# Revit family: Rohrschelle Trabant Inox, M 8-M10, ohne Dämmung, V4A
name_source: partatom
category: HLS-Bauteile
revit_build: Autodesk Revit 2017 (Build: 20190507_1515(x64)
units: mm (PartAtom-declared; Revit-internal decimal feet)

## family parameters
Arbeitsebenenbasiert = Ja
Beim Laden mit Abzugskörper schneiden = Nein
Bemaßung runder Anschluss = Durchmesser verwenden
Gemeinsam genutzt = Ja
Immer vertikal = Nein
Raumberechnungspunkt = Nein
Teiletyp = Normal

## types (11) — shared parameters
Anschluss = M8/M10
Bauart = zweiteilig
DF2 = 16 mm  [stored 0.0524934 ft]
DVS = 5 mm  [stored 0.0164042 ft]
Fabrikat = MEFA
Firma = MEFA Befestigungs- und Montagesysteme GmbH
H1 = 2 mm  [stored 0.00656168 ft]
HGA = 17 mm
Material = Edelstahl
Mengeneinheit = St
Verschluss = Rastverschluss
Verschluss-Schraube = M6
Vorgabe-Ansicht = 1219 mm
max. zul. Last horizontal = 0.00 kN
max. zul. Last vertikal = 0.00 kN
zero-valued in all types: DS, Nennweite DN Rohr, Rohraußendurchmesser

## per-type parameters (varying)
- Trabant Inox, M8/M10, Ø 21- 24, o.Gummi, V4A: A=18 mm  [stored 0.0590551 ft]; AB=3 mm  [stored 0.00984252 ft]; Achsabstand=42,0 mm; Anschlußhöhe=17,5 mm; Artikelnummer=051005024; B=59 mm; Breite Material=20 mm; D=24 mm  [stored 0.0787402 ft]; D0=24 mm  [stored 0.0787402 ft]; DF1=17 mm; Dmax=24 mm  [stored 0.0787402 ft]; Dmin=21 mm  [stored 0.0688976 ft]; EAN=4250928454003; Gewicht=0.05 kg; Gewicht pro Bauteil=0.05 kg; H=43 mm  [stored 0.141076 ft]; H2=4 mm  [stored 0.0131234 ft]; Kurztext1=Rohrschelle Trabant Inox 20x1,0; Kurztext2=21 - 24 mm M8/M10; MB=20 mm  [stored 0.0656168 ft]; MD=1 mm  [stored 0.00328084 ft]; Materialmaße=20x1,0 mm; R=12 mm  [stored 0.0393701 ft]; RM=15 mm  [stored 0.0492126 ft]; Rohraußendurchmesser Zoll=1/2 Zoll; S=42 mm  [stored 0.137795 ft]; Stärke Material=1 mm  [stored 0.00328084 ft]; max. Rohraußendurchmesser=24 mm  [stored 0.0787402 ft]; min. Rohraußendurchmesser=21 mm  [stored 0.0688976 ft]; vpe=100 St
- Trabant Inox, M8/M10, Ø 25- 29, o.Gummi, V4A: A=18 mm  [stored 0.0590551 ft]; AB=4 mm  [stored 0.0131234 ft]; Achsabstand=46,5 mm; Anschlußhöhe=17,5 mm; Artikelnummer=051005029; B=64 mm; Breite Material=20 mm; D=29 mm  [stored 0.0951444 ft]; D0=29 mm  [stored 0.0951444 ft]; DF1=17 mm; Dmax=29 mm  [stored 0.0951444 ft]; Dmin=25 mm  [stored 0.082021 ft]; EAN=4250928454010; Gewicht=0.05 kg; Gewicht pro Bauteil=0.05 kg; H=48 mm  [stored 0.15748 ft]; H2=5 mm  [stored 0.0164042 ft]; Kurztext1=Rohrschelle Trabant Inox 20x1,0; Kurztext2=25 - 29 mm M8/M10; MB=20 mm  [stored 0.0656168 ft]; MD=1 mm  [stored 0.00328084 ft]; Materialmaße=20x1,0 mm; R=15 mm  [stored 0.0492126 ft]; RM=18 mm  [stored 0.0590551 ft]; Rohraußendurchmesser Zoll=3/4 Zoll; S=47 mm  [stored 0.154199 ft]; Stärke Material=1 mm  [stored 0.00328084 ft]; max. Rohraußendurchmesser=29 mm  [stored 0.0951444 ft]; min. Rohraußendurchmesser=25 mm  [stored 0.082021 ft]; vpe=100 St
- Trabant Inox, M8/M10, Ø 30- 34, o.Gummi, V4A: A=18 mm  [stored 0.0590551 ft]; AB=4 mm  [stored 0.0131234 ft]; Achsabstand=51,5 mm; Anschlußhöhe=17,5 mm; Artikelnummer=051005034; B=69 mm; Breite Material=20 mm; D=34 mm  [stored 0.111549 ft]; D0=34 mm  [stored 0.111549 ft]; DF1=17 mm; Dmax=34 mm  [stored 0.111549 ft]; Dmin=30 mm  [stored 0.0984252 ft]; EAN=4250928454027; Gewicht=0.05 kg; Gewicht pro Bauteil=0.05 kg; H=53 mm; H2=5 mm  [stored 0.0164042 ft]; Kurztext1=Rohrschelle Trabant Inox 20x1,0; Kurztext2=30 - 34 mm M8/M10; MB=20 mm  [stored 0.0656168 ft]; MD=1 mm  [stored 0.00328084 ft]; Materialmaße=20x1,0 mm; R=17 mm; RM=20 mm  [stored 0.0656168 ft]; Rohraußendurchmesser Zoll=1 Zoll; S=52 mm; Stärke Material=1 mm  [stored 0.00328084 ft]; max. Rohraußendurchmesser=34 mm  [stored 0.111549 ft]; min. Rohraußendurchmesser=30 mm  [stored 0.0984252 ft]; vpe=100 St
- Trabant Inox, M8/M10, Ø 35- 39, o.Gummi, V4A: A=18 mm  [stored 0.0590551 ft]; AB=4 mm  [stored 0.0131234 ft]; Achsabstand=57,0 mm; Anschlußhöhe=17,5 mm; Artikelnummer=051005039; B=74 mm; Breite Material=20 mm; D=39 mm  [stored 0.127953 ft]; D0=39 mm  [stored 0.127953 ft]; DF1=17 mm; Dmax=39 mm  [stored 0.127953 ft]; Dmin=35 mm  [stored 0.114829 ft]; EAN=4250928454034; Gewicht=0.05 kg; Gewicht pro Bauteil=0.05 kg; H=58 mm; H2=5 mm  [stored 0.0164042 ft]; Kurztext1=Rohrschelle Trabant Inox 20x1,0; Kurztext2=35 - 39 mm M8/M10; MB=20 mm  [stored 0.0656168 ft]; MD=1 mm  [stored 0.00328084 ft]; Materialmaße=20x1,0 mm; R=20 mm  [stored 0.0656168 ft]; RM=23 mm; S=57 mm; Stärke Material=1 mm  [stored 0.00328084 ft]; max. Rohraußendurchmesser=39 mm  [stored 0.127953 ft]; min. Rohraußendurchmesser=35 mm  [stored 0.114829 ft]; vpe=100 St
- Trabant Inox, M8/M10, Ø 41- 48, o.Gummi, V4A: A=18 mm  [stored 0.0590551 ft]; AB=7 mm  [stored 0.0229659 ft]; Achsabstand=65,0 mm; Anschlußhöhe=17,5 mm; Artikelnummer=051005048; B=83 mm; Breite Material=20 mm; D=48 mm  [stored 0.15748 ft]; D0=48 mm  [stored 0.15748 ft]; DF1=17 mm; Dmax=48 mm  [stored 0.15748 ft]; Dmin=41 mm  [stored 0.134514 ft]; EAN=4250928454041; Gewicht=0.06 kg; Gewicht pro Bauteil=0.06 kg; H=67 mm; H2=6 mm  [stored 0.019685 ft]; Kurztext1=Rohrschelle Trabant Inox 20x1,0; Kurztext2=41 - 48 mm M8/M10; MB=20 mm  [stored 0.0656168 ft]; MD=1 mm  [stored 0.00328084 ft]; Materialmaße=20x1,0 mm; R=24 mm  [stored 0.0787402 ft]; RM=29 mm  [stored 0.0951444 ft]; Rohraußendurchmesser Zoll=1 1/4 Zoll; S=66 mm; Stärke Material=1 mm  [stored 0.00328084 ft]; max. Rohraußendurchmesser=48 mm  [stored 0.15748 ft]; min. Rohraußendurchmesser=41 mm  [stored 0.134514 ft]; vpe=100 St
- Trabant Inox, M8/M10, Ø 51- 55, o.Gummi, V4A: A=19 mm; AB=4 mm  [stored 0.0131234 ft]; Achsabstand=74,0 mm; Anschlußhöhe=18 mm; Artikelnummer=051005055; B=92 mm; Breite Material=20 mm; D=55 mm; D0=55 mm; DF1=18 mm  [stored 0.0590551 ft]; Dmax=55 mm; Dmin=51 mm  [stored 0.167323 ft]; EAN=4250928454058; Gewicht=0.08 kg; Gewicht pro Bauteil=0.08 kg; H=75 mm; H2=5 mm  [stored 0.0164042 ft]; Kurztext1=Rohrschelle Trabant Inox 20x1,5; Kurztext2=51 - 55 mm M8/M10; MB=20 mm  [stored 0.0656168 ft]; MD=2 mm  [stored 0.00656168 ft]; Materialmaße=20x1,5 mm; R=28 mm; RM=31 mm  [stored 0.101706 ft]; Rohraußendurchmesser Zoll=1 1/2 Zoll; S=74 mm; Stärke Material=2 mm  [stored 0.00656168 ft]; max. Rohraußendurchmesser=55 mm; min. Rohraußendurchmesser=51 mm  [stored 0.167323 ft]; vpe=50 St
- Trabant Inox, M8/M10, Ø 57- 61, o.Gummi, V4A: A=19 mm; AB=4 mm  [stored 0.0131234 ft]; Achsabstand=80,5 mm; Anschlußhöhe=18 mm; Artikelnummer=051005061; B=98 mm; Breite Material=20 mm; D=61 mm; D0=61 mm; DF1=18 mm  [stored 0.0590551 ft]; Dmax=61 mm; Dmin=57 mm; EAN=4250928454065; Gewicht=0.09 kg; Gewicht pro Bauteil=0.09 kg; H=81 mm; H2=5 mm  [stored 0.0164042 ft]; Kurztext1=Rohrschelle Trabant Inox 20x1,5; Kurztext2=57 - 61 mm M8/M10; MB=20 mm  [stored 0.0656168 ft]; MD=2 mm  [stored 0.00656168 ft]; Materialmaße=20x1,5 mm; R=31 mm  [stored 0.101706 ft]; RM=34 mm  [stored 0.111549 ft]; Rohraußendurchmesser Zoll=2 Zoll; S=80 mm; Stärke Material=2 mm  [stored 0.00656168 ft]; max. Rohraußendurchmesser=61 mm; min. Rohraußendurchmesser=57 mm; vpe=50 St
- Trabant Inox, M8/M10, Ø 63- 67, o.Gummi, V4A: A=19 mm; AB=4 mm  [stored 0.0131234 ft]; Achsabstand=86,5 mm; Anschlußhöhe=18 mm; Artikelnummer=051005067; B=104 mm; Breite Material=20 mm; D=67 mm; D0=67 mm; DF1=18 mm  [stored 0.0590551 ft]; Dmax=67 mm; Dmin=63 mm; EAN=4250928454072; Gewicht=0.09 kg; Gewicht pro Bauteil=0.09 kg; H=87 mm; H2=5 mm  [stored 0.0164042 ft]; Kurztext1=Rohrschelle Trabant Inox 20x1,5; Kurztext2=63 - 67 mm M8/M10; MB=20 mm  [stored 0.0656168 ft]; MD=2 mm  [stored 0.00656168 ft]; Materialmaße=20x1,5 mm; R=34 mm  [stored 0.111549 ft]; RM=37 mm  [stored 0.121391 ft]; S=86 mm; Stärke Material=2 mm  [stored 0.00656168 ft]; max. Rohraußendurchmesser=67 mm; min. Rohraußendurchmesser=63 mm; vpe=50 St
- Trabant Inox, M8/M10, Ø 69- 74, o.Gummi, V4A: A=19 mm; AB=5 mm  [stored 0.0164042 ft]; Achsabstand=93,5 mm; Anschlußhöhe=18 mm; Artikelnummer=051005074; B=111 mm; Breite Material=20 mm; D=74 mm; D0=74 mm; DF1=18 mm  [stored 0.0590551 ft]; Dmax=74 mm; Dmin=69 mm; EAN=4250928454089; Gewicht=0.10 kg; Gewicht pro Bauteil=0.10 kg; H=94 mm; H2=6 mm  [stored 0.019685 ft]; Kurztext1=Rohrschelle Trabant Inox 20x1,5; Kurztext2=69 - 74 mm M8/M10; MB=20 mm  [stored 0.0656168 ft]; MD=2 mm  [stored 0.00656168 ft]; Materialmaße=20x1,5 mm; R=37 mm  [stored 0.121391 ft]; RM=41 mm  [stored 0.134514 ft]; S=93 mm; Stärke Material=2 mm  [stored 0.00656168 ft]; max. Rohraußendurchmesser=74 mm; min. Rohraußendurchmesser=69 mm; vpe=50 St
- Trabant Inox, M8/M10, Ø 76- 85, o.Gummi, V4A: A=19 mm; AB=9 mm  [stored 0.0295276 ft]; Achsabstand=104,0 mm; Anschlußhöhe=18 mm; Artikelnummer=051005085; B=121 mm; Breite Material=25 mm; D=85 mm; D0=85 mm; DF1=17 mm; Dmax=85 mm; Dmin=76 mm; EAN=4250928454096; Gewicht=0.12 kg; Gewicht pro Bauteil=0.12 kg; H=105 mm; H2=8 mm  [stored 0.0262467 ft]; Kurztext1=Rohrschelle Trabant Inox 25x1,5; Kurztext2=76 - 85 mm M8/M10; MB=25 mm  [stored 0.082021 ft]; MD=2 mm  [stored 0.00656168 ft]; Materialmaße=25x1,5 mm; R=43 mm  [stored 0.141076 ft]; RM=49 mm; Rohraußendurchmesser Zoll=2 1/2 Zoll; S=104 mm; Stärke Material=2 mm  [stored 0.00656168 ft]; max. Rohraußendurchmesser=85 mm; min. Rohraußendurchmesser=76 mm; vpe=50 St
- Trabant Inox, M8/M10, Ø 84- 90, o.Gummi, V4A: A=19 mm; AB=6 mm  [stored 0.019685 ft]; Achsabstand=109,0 mm; Anschlußhöhe=18 mm; Artikelnummer=051005090; B=126 mm; Breite Material=25 mm; D=90 mm; D0=90 mm; DF1=17 mm; Dmax=90 mm; Dmin=84 mm; EAN=4250928454102; Gewicht=0.13 kg; Gewicht pro Bauteil=0.13 kg; H=110 mm; H2=6 mm  [stored 0.019685 ft]; Kurztext1=Rohrschelle Trabant Inox 25x1,5; Kurztext2=84 - 90 mm M8/M10; MB=25 mm  [stored 0.082021 ft]; MD=2 mm  [stored 0.00656168 ft]; Materialmaße=25x1,5 mm; R=45 mm  [stored 0.147638 ft]; RM=50 mm  [stored 0.164042 ft]; Rohraußendurchmesser Zoll=3 Zoll; S=109 mm; Stärke Material=2 mm  [stored 0.00656168 ft]; max. Rohraußendurchmesser=90 mm; min. Rohraußendurchmesser=84 mm; vpe=50 St

note: [stored X ft] marks values corroborated as IEEE doubles in the binary element streams (Revit-internal decimal feet)

## geometry (parser evidence)
native form markers: Sweep x3
no freeform markers — native parametric forms only
